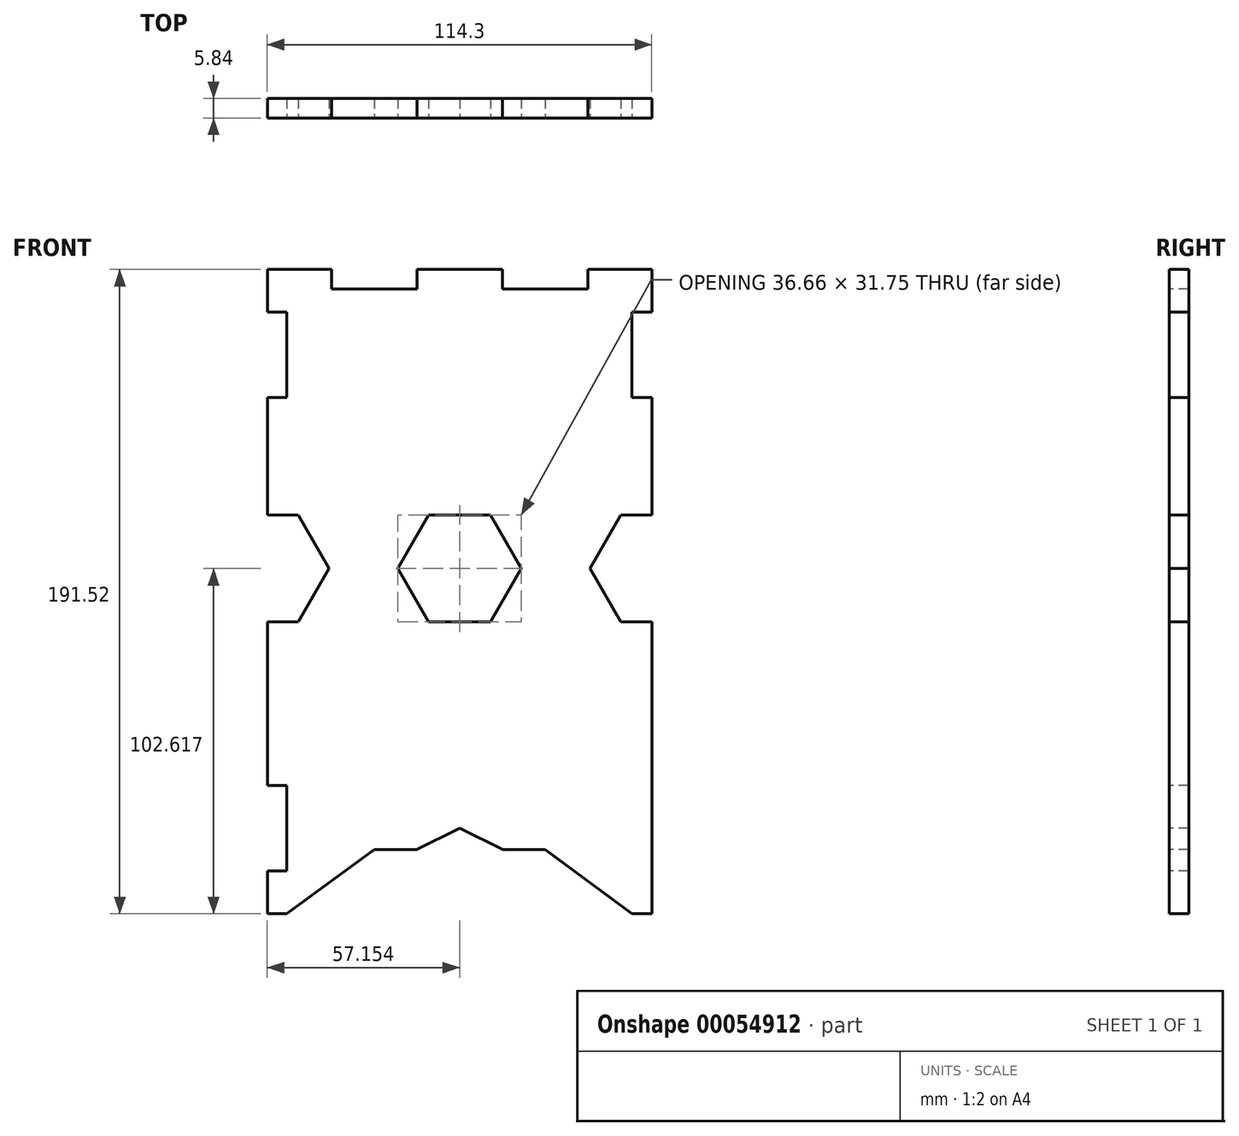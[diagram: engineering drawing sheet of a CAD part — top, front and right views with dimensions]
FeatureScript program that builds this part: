
annotation { "Feature Type Name" : "Feature", "Feature Type Description" : "" }
export const myFeature = defineFeature(function(context is Context, id is Id, definition is map)
    precondition{}
    {
        {
            var Q0;
            Q0=qCreatedBy(makeId("Front.planeOp"),FACE);
            var sketch = newSketch(context, id + "F0", { "sketchPlane" : qUnion([Q0])});
            skLineSegment(sketch, "E0.bottom", {"start": v(-70.35, 29.62) * mm, "end": v(43.95, 29.62) * mm});
            skLineSegment(sketch, "E0.top", {"start": v(-70.35, -161.9) * mm, "end": v(43.95, -161.9) * mm});
            skLineSegment(sketch, "E0.left", {"start": v(-70.35, 29.62) * mm, "end": v(-70.35, -161.9) * mm});
            skLineSegment(sketch, "E0.right", {"start": v(43.95, 29.62) * mm, "end": v(43.95, -161.9) * mm});
            skSolve(sketch);
        }
        {
            var Q0;
            Q0=makeQuery(id+"F0.imprint","IMPRINT",FACE,{"disambiguationData":[TD([[makeQuery(id+"F0.imprint","IMPRINT",EDGE,{"derivedFrom":sQuery(id+"F0.wireOp",EDGE,"E0.bottom")}),-1.0]])]});
            extrude(context, id + "F1", {"entities" : qUnion([Q0]), "oppositeDirection" : true, "depth" : 5.84 * mm});
        }
        {
            var Q0;
            Q0=makeQuery(id+"F1.opExtrude","CAP_FACE",FACE,{"disambiguationData":[OSD([sQuery(id+"F0.wireOp",EDGE,"E0.bottom"),sQuery(id+"F0.wireOp",EDGE,"E0.top"),sQuery(id+"F0.wireOp",EDGE,"E0.left"),sQuery(id+"F0.wireOp",EDGE,"E0.right")])],"isStart":true});
            var sketch = newSketch(context, id + "F2", { "sketchPlane" : qUnion([Q0])});
            skPoint(sketch, "E1", {"position": v(-13.2, 29.62) * mm});
            skLineSegment(sketch, "E2.bottom", {"start": v(-70.35, 16.92) * mm, "end": v(-64.5, 16.92) * mm});
            skLineSegment(sketch, "E2.top", {"start": v(-70.35, -8.48) * mm, "end": v(-64.5, -8.48) * mm});
            skLineSegment(sketch, "E2.left", {"start": v(-70.35, 16.92) * mm, "end": v(-70.35, -8.48) * mm});
            skLineSegment(sketch, "E2.right", {"start": v(-64.5, 16.92) * mm, "end": v(-64.5, -8.48) * mm});
            skLineSegment(sketch, "E3.bottom", {"start": v(-70.35, -149.2) * mm, "end": v(-64.5, -149.2) * mm});
            skLineSegment(sketch, "E3.top", {"start": v(-70.35, -123.8) * mm, "end": v(-64.5, -123.8) * mm});
            skLineSegment(sketch, "E3.left", {"start": v(-70.35, -149.2) * mm, "end": v(-70.35, -123.8) * mm});
            skLineSegment(sketch, "E3.right", {"start": v(-64.5, -149.2) * mm, "end": v(-64.5, -123.8) * mm});
            skLineSegment(sketch, "E4.bottom", {"start": v(43.95, -8.48) * mm, "end": v(38.11, -8.48) * mm});
            skLineSegment(sketch, "E4.top", {"start": v(43.95, 16.92) * mm, "end": v(38.11, 16.92) * mm});
            skLineSegment(sketch, "E4.left", {"start": v(43.95, -8.48) * mm, "end": v(43.95, 16.92) * mm});
            skLineSegment(sketch, "E4.right", {"start": v(38.11, -8.48) * mm, "end": v(38.11, 16.92) * mm});
            skLineSegment(sketch, "E5.bottom", {"start": v(-51.3, 29.62) * mm, "end": v(-25.9, 29.62) * mm});
            skLineSegment(sketch, "E5.top", {"start": v(-51.3, 23.77) * mm, "end": v(-25.9, 23.77) * mm});
            skLineSegment(sketch, "E5.left", {"start": v(-51.3, 29.62) * mm, "end": v(-51.3, 23.77) * mm});
            skLineSegment(sketch, "E5.right", {"start": v(-25.9, 29.62) * mm, "end": v(-25.9, 23.77) * mm});
            skLineSegment(sketch, "E6.bottom", {"start": v(24.9, 29.62) * mm, "end": v(-0.5, 29.62) * mm});
            skLineSegment(sketch, "E6.top", {"start": v(24.9, 23.77) * mm, "end": v(-0.5, 23.77) * mm});
            skLineSegment(sketch, "E6.left", {"start": v(24.9, 29.62) * mm, "end": v(24.9, 23.77) * mm});
            skLineSegment(sketch, "E6.right", {"start": v(-0.5, 29.62) * mm, "end": v(-0.5, 23.77) * mm});
            skLineSegment(sketch, "E7", {"start": v(-70.35, -59.28) * mm, "end": v(43.95, -59.28) * mm, "construction": true});
            skCircle(sketch, "E8.cCircle", {"center": v(-70.35, -59.28) * mm, "radius": 15.88 * mm, "construction": true});
            skLineSegment(sketch, "E8.0", {"start": v(-79.51, -43.4) * mm, "end": v(-61.18, -43.4) * mm});
            skLineSegment(sketch, "E8.1", {"start": v(-61.18, -43.4) * mm, "end": v(-52.01, -59.28) * mm});
            skLineSegment(sketch, "E8.2", {"start": v(-52.01, -59.28) * mm, "end": v(-61.18, -75.16) * mm});
            skLineSegment(sketch, "E8.3", {"start": v(-61.18, -75.16) * mm, "end": v(-79.51, -75.16) * mm});
            skLineSegment(sketch, "E8.4", {"start": v(-79.51, -75.16) * mm, "end": v(-88.68, -59.28) * mm});
            skLineSegment(sketch, "E8.5", {"start": v(-88.68, -59.28) * mm, "end": v(-79.51, -43.4) * mm});
            skPoint(sketch, "E8.0.midPoint", {"position": v(-70.35, -43.4) * mm});
            skCircle(sketch, "E9.cCircle", {"center": v(43.95, -59.28) * mm, "radius": 15.88 * mm, "construction": true});
            skLineSegment(sketch, "E9.0", {"start": v(34.79, -43.4) * mm, "end": v(53.12, -43.4) * mm});
            skLineSegment(sketch, "E9.1", {"start": v(53.12, -43.4) * mm, "end": v(62.29, -59.28) * mm});
            skLineSegment(sketch, "E9.2", {"start": v(62.29, -59.28) * mm, "end": v(53.12, -75.16) * mm});
            skLineSegment(sketch, "E9.3", {"start": v(53.12, -75.16) * mm, "end": v(34.79, -75.16) * mm});
            skLineSegment(sketch, "E9.4", {"start": v(34.79, -75.16) * mm, "end": v(25.62, -59.28) * mm});
            skLineSegment(sketch, "E9.5", {"start": v(25.62, -59.28) * mm, "end": v(34.79, -43.4) * mm});
            skPoint(sketch, "E9.0.midPoint", {"position": v(43.95, -43.4) * mm});
            skPoint(sketch, "E10", {"position": v(-64.5, -161.9) * mm});
            skPoint(sketch, "E11", {"position": v(38.11, -161.9) * mm});
            skLineSegment(sketch, "E12", {"start": v(-64.5, -161.9) * mm, "end": v(-13.2, -136.5) * mm});
            skLineSegment(sketch, "E13", {"start": v(-13.2, -136.5) * mm, "end": v(38.11, -161.9) * mm});
            skLineSegment(sketch, "E14", {"start": v(-64.5, -161.9) * mm, "end": v(-38.6, -142.85) * mm});
            skLineSegment(sketch, "E15", {"start": v(-38.6, -142.85) * mm, "end": v(12.2, -142.85) * mm});
            skLineSegment(sketch, "E16", {"start": v(12.2, -142.85) * mm, "end": v(38.11, -161.9) * mm});
            skPoint(sketch, "E17", {"position": v(-38.6, 23.77) * mm});
            skPoint(sketch, "E18", {"position": v(12.2, 23.77) * mm});
            skSolve(sketch);
        }
        {
            var Q0;
            Q0=makeQuery(id+"F2.imprint","IMPRINT",FACE,{"disambiguationData":[TD([[makeQuery(id+"F2.imprint","IMPRINT",EDGE,{"derivedFrom":sQuery(id+"F2.wireOp",EDGE,"e04a2969-19e7-41b5-8507-a6da88226fcc")}),1.0]])]});
            var Q1;
            Q1=makeQuery(id+"F2.imprint","IMPRINT",FACE,{"disambiguationData":[TD([[makeQuery(id+"F2.imprint","IMPRINT",EDGE,{"derivedFrom":sQuery(id+"F2.wireOp",EDGE,"2b5f83f8-09b8-4e4b-9822-bfe2e90a324b")}),-1.0]])]});
            var Q2;
            {var subQ0=sQuery(id+"F2.wireOp",EDGE,"6b19a64c-c84a-4c8d-bff8-ca71bc347f0d");var subQ1=makeQuery(id+"F1.opExtrude","CAP_EDGE",EDGE,{"disambiguationData":[OSD([sQuery(id+"F0.wireOp",EDGE,"E0.left")])],"isStart":true});var subQ2=makeQuery(id+"F2.imprint","INTERSECT",VERTEX,{"disambiguationData":[OD(0.0)],"derivedFrom":[subQ1,subQ0]});Q2=makeQuery(id+"F2.imprint","IMPRINT",FACE,{"disambiguationData":[TD([[makeQuery(id+"F2.imprint","IMPRINT",EDGE,{"disambiguationData":[TD([[subQ2,1.0]])],"derivedFrom":subQ0}),1.0]])]});}
            var Q3;
            {var subQ0=sQuery(id+"F2.wireOp",EDGE,"bff67b8d-5e5b-4b84-a925-2c33a9d24f48");var subQ1=makeQuery(id+"F1.opExtrude","CAP_EDGE",EDGE,{"disambiguationData":[OSD([sQuery(id+"F0.wireOp",EDGE,"E0.right")])],"isStart":true});var subQ2=makeQuery(id+"F2.imprint","INTERSECT",VERTEX,{"disambiguationData":[OD(0.0)],"derivedFrom":[subQ1,subQ0]});Q3=makeQuery(id+"F2.imprint","IMPRINT",FACE,{"disambiguationData":[TD([[makeQuery(id+"F2.imprint","IMPRINT",EDGE,{"disambiguationData":[TD([[subQ2,-1.0]])],"derivedFrom":subQ0}),1.0]])]});}
            var Q4;
            Q4=makeQuery(id+"F2.imprint","IMPRINT",FACE,{"disambiguationData":[TD([[makeQuery(id+"F2.imprint","IMPRINT",EDGE,{"derivedFrom":sQuery(id+"F2.wireOp",EDGE,"E2.bottom")}),-1.0]])]});
            var Q5;
            Q5=makeQuery(id+"F2.imprint","IMPRINT",FACE,{"disambiguationData":[TD([[makeQuery(id+"F2.imprint","IMPRINT",EDGE,{"derivedFrom":sQuery(id+"F2.wireOp",EDGE,"E3.bottom")}),1.0]])]});
            var Q6;
            Q6=makeQuery(id+"F2.imprint","IMPRINT",FACE,{"disambiguationData":[TD([[makeQuery(id+"F2.imprint","IMPRINT",EDGE,{"derivedFrom":sQuery(id+"F2.wireOp",EDGE,"E4.bottom")}),-1.0]])]});
            var Q7;
            {var subQ0=sQuery(id+"F2.wireOp",EDGE,"bff67b8d-5e5b-4b84-a925-2c33a9d24f48");var subQ1=makeQuery(id+"F1.opExtrude","CAP_EDGE",EDGE,{"disambiguationData":[OSD([sQuery(id+"F0.wireOp",EDGE,"E0.right")])],"isStart":true});var subQ2=makeQuery(id+"F2.imprint","INTERSECT",VERTEX,{"disambiguationData":[OD(0.0)],"derivedFrom":[subQ1,subQ0]});Q7=makeQuery(id+"F2.imprint","IMPRINT",FACE,{"disambiguationData":[TD([[makeQuery(id+"F2.imprint","IMPRINT",EDGE,{"disambiguationData":[TD([[subQ2,1.0]])],"derivedFrom":subQ0}),1.0]])]});}
            var Q8;
            Q8=makeQuery(id+"F2.imprint","IMPRINT",FACE,{"disambiguationData":[TD([[makeQuery(id+"F2.imprint","IMPRINT",EDGE,{"derivedFrom":sQuery(id+"F2.wireOp",EDGE,"E5.bottom")}),-1.0]])]});
            var Q9;
            Q9=makeQuery(id+"F2.imprint","IMPRINT",FACE,{"disambiguationData":[TD([[makeQuery(id+"F2.imprint","IMPRINT",EDGE,{"derivedFrom":sQuery(id+"F2.wireOp",EDGE,"E6.bottom")}),-1.0]])]});
            var Q10;
            {var subQ1=sQuery(id+"F2.wireOp",EDGE,"E8.4");Q10=makeQuery(id+"F2.imprint","IMPRINT",FACE,{"disambiguationData":[TD([[makeQuery(id+"F2.imprint","IMPRINT",EDGE,{"derivedFrom":subQ1}),-1.0]])]});}
            var Q11;
            {var subQ4=sQuery(id+"F2.wireOp",EDGE,"E8.1");Q11=makeQuery(id+"F2.imprint","IMPRINT",FACE,{"disambiguationData":[TD([[makeQuery(id+"F2.imprint","IMPRINT",EDGE,{"derivedFrom":subQ4}),-1.0]])]});}
            var Q12;
            {var subQ4=sQuery(id+"F2.wireOp",EDGE,"E9.4");Q12=makeQuery(id+"F2.imprint","IMPRINT",FACE,{"disambiguationData":[TD([[makeQuery(id+"F2.imprint","IMPRINT",EDGE,{"derivedFrom":subQ4}),-1.0]])]});}
            var Q13;
            {var subQ4=sQuery(id+"F2.wireOp",EDGE,"E9.1");Q13=makeQuery(id+"F2.imprint","IMPRINT",FACE,{"disambiguationData":[TD([[makeQuery(id+"F2.imprint","IMPRINT",EDGE,{"derivedFrom":subQ4}),-1.0]])]});}
            var Q14;
            Q14=makeQuery(id+"F2.imprint","IMPRINT",FACE,{"disambiguationData":[TD([[makeQuery(id+"F2.imprint","IMPRINT",EDGE,{"derivedFrom":sQuery(id+"F2.wireOp",EDGE,"2oQqyDtO-3jd9-5Rg8-UYLx-3pKa0KnkSeOB")}),-1.0]])]});
            var Q15;
            {var subQ0=sQuery(id+"F2.wireOp",EDGE,"E12");Q15=makeQuery(id+"F2.imprint","IMPRINT",FACE,{"disambiguationData":[TD([[makeQuery(id+"F2.imprint","IMPRINT",EDGE,{"derivedFrom":subQ0}),-1.0]])]});}
            var Q16;
            {var subQ0=sQuery(id+"F2.wireOp",EDGE,"E12");var subQ3=sQuery(id+"F2.wireOp",EDGE,"E15");var subQ4=makeQuery(id+"F2.imprint","INTERSECT",VERTEX,{"derivedFrom":[subQ0,subQ3]});Q16=makeQuery(id+"F2.imprint","IMPRINT",FACE,{"disambiguationData":[TD([[makeQuery(id+"F2.imprint","IMPRINT",EDGE,{"disambiguationData":[TD([[subQ4,-1.0]])],"derivedFrom":subQ3}),-1.0]])]});}
            var Q17;
            {var subQ0=sQuery(id+"F2.wireOp",EDGE,"E14");Q17=makeQuery(id+"F2.imprint","IMPRINT",FACE,{"disambiguationData":[TD([[makeQuery(id+"F2.imprint","IMPRINT",EDGE,{"derivedFrom":subQ0}),-1.0]])]});}
            var Q18;
            {var subQ0=sQuery(id+"F2.wireOp",EDGE,"E16");Q18=makeQuery(id+"F2.imprint","IMPRINT",FACE,{"disambiguationData":[TD([[makeQuery(id+"F2.imprint","IMPRINT",EDGE,{"derivedFrom":subQ0}),-1.0]])]});}
            var Q19;
            Q19=makeQuery(id+"F1.opExtrude","CAP_FACE",FACE,{"disambiguationData":[OSD([sQuery(id+"F0.wireOp",EDGE,"E0.bottom"),sQuery(id+"F0.wireOp",EDGE,"E0.top"),sQuery(id+"F0.wireOp",EDGE,"E0.left"),sQuery(id+"F0.wireOp",EDGE,"E0.right")])],"isStart":false});
            extrude(context, id + "F3", {"entities" : qUnion([Q0, Q1, Q2, Q3, Q4, Q5, Q6, Q7, Q8, Q9, Q10, Q11, Q12, Q13, Q14, Q15, Q16, Q17, Q18]), "operationType" : NewBodyOperationType.REMOVE, "endBound" : BoundingType.UP_TO_SURFACE, "oppositeDirection" : true, "endBoundEntityFace" : qUnion([Q19]), "depth" : 25.4 * mm});
        }
        {
            var Q0;
            Q0=makeQuery(id+"F1.opExtrude","CAP_FACE",FACE,{"disambiguationData":[OSD([sQuery(id+"F0.wireOp",EDGE,"E0.bottom"),sQuery(id+"F0.wireOp",EDGE,"E0.top"),sQuery(id+"F0.wireOp",EDGE,"E0.left"),sQuery(id+"F0.wireOp",EDGE,"E0.right")])],"isStart":true});
            var sketch = newSketch(context, id + "F4", { "sketchPlane" : qUnion([Q0])});
            skCircle(sketch, "E19.cCircle", {"center": v(-13.2, -59.28) * mm, "radius": 15.88 * mm, "construction": true});
            skLineSegment(sketch, "E19.0", {"start": v(-4.03, -43.4) * mm, "end": v(5.14, -59.28) * mm});
            skLineSegment(sketch, "E19.1", {"start": v(5.14, -59.28) * mm, "end": v(-4.03, -75.16) * mm});
            skLineSegment(sketch, "E19.2", {"start": v(-4.03, -75.16) * mm, "end": v(-22.36, -75.16) * mm});
            skLineSegment(sketch, "E19.3", {"start": v(-22.36, -75.16) * mm, "end": v(-31.53, -59.28) * mm});
            skLineSegment(sketch, "E19.4", {"start": v(-31.53, -59.28) * mm, "end": v(-22.36, -43.4) * mm});
            skLineSegment(sketch, "E19.5", {"start": v(-22.36, -43.4) * mm, "end": v(-4.03, -43.4) * mm});
            skPoint(sketch, "E19.0.midPoint", {"position": v(0.55, -51.35) * mm});
            skLineSegment(sketch, "E20", {"start": v(-13.2, 29.62) * mm, "end": v(-13.2, -159.96) * mm, "construction": true});
            skLineSegment(sketch, "E21", {"start": v(-52.01, -59.28) * mm, "end": v(25.62, -59.28) * mm, "construction": true});
            skSolve(sketch);
        }
        {
            var Q0;
            Q0=makeQuery(id+"F4.imprint","IMPRINT",FACE,{"disambiguationData":[TD([[makeQuery(id+"F4.imprint","IMPRINT",EDGE,{"derivedFrom":sQuery(id+"F4.wireOp",EDGE,"E19.0")}),-1.0]])]});
            var Q1;
            Q1=makeQuery(id+"F1.opExtrude","CAP_FACE",FACE,{"disambiguationData":[OSD([sQuery(id+"F0.wireOp",EDGE,"E0.bottom"),sQuery(id+"F0.wireOp",EDGE,"E0.top"),sQuery(id+"F0.wireOp",EDGE,"E0.left"),sQuery(id+"F0.wireOp",EDGE,"E0.right")])],"isStart":false});
            extrude(context, id + "F5", {"entities" : qUnion([Q0]), "operationType" : NewBodyOperationType.REMOVE, "endBound" : BoundingType.UP_TO_SURFACE, "oppositeDirection" : true, "endBoundEntityFace" : qUnion([Q1]), "depth" : 25.4 * mm});
        }
    });
